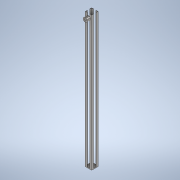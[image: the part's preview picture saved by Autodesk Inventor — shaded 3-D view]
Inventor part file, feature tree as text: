
AUTODESK INVENTOR PART (.ipt)
format: ipt  version: 2020 (Build 240168000, 168)  size: 163,328 bytes
history: native  units: mm
features: extrude x6, sketch x6
ambient origin geometry x8: Origin, YZ Plane, XZ Plane, XY Plane, X Axis, Y Axis, Z Axis, Center Point
bodies: Solid1 (feature_tree)
feature tree (12):
  extrude  "Extrusion1"  Depth=38.0mm
  extrude  "Extrusion5"  Depth=800.0mm TaperAngle=0.0deg
  sketch  "Sketch6"  dims[d20=15.0mm d21=55.0mm]
  extrude  "Extrusion6"  Depth=15.0mm
  extrude  "Extrusion7"  Depth=15.0mm
  extrude  "Extrusion8"  Depth=35.0mm
  extrude  "Extrusion9"  Depth=800.0mm TaperAngle=0.0deg
  sketch  "Sketch1"  dims[d0=38.0mm d1=38.0mm]
  sketch  "Sketch5"  dims[d2=5.0mm d3=0.0mm d18=800.0mm d19=0.0mm]
  sketch  "Sketch7"  dims[d22=55.0mm d23=15.0mm]
  sketch  "Sketch8"  dims[d24=35.0mm d25=35.0mm]
  sketch  "Sketch9"  dims[d26=800.0mm d27=0.0mm d28=800.0mm d29=0.0mm d30=10.0mm d31=2.0mm d32=0.0mm d33=13.0mm d34=20.0mm d35=0.0mm]
